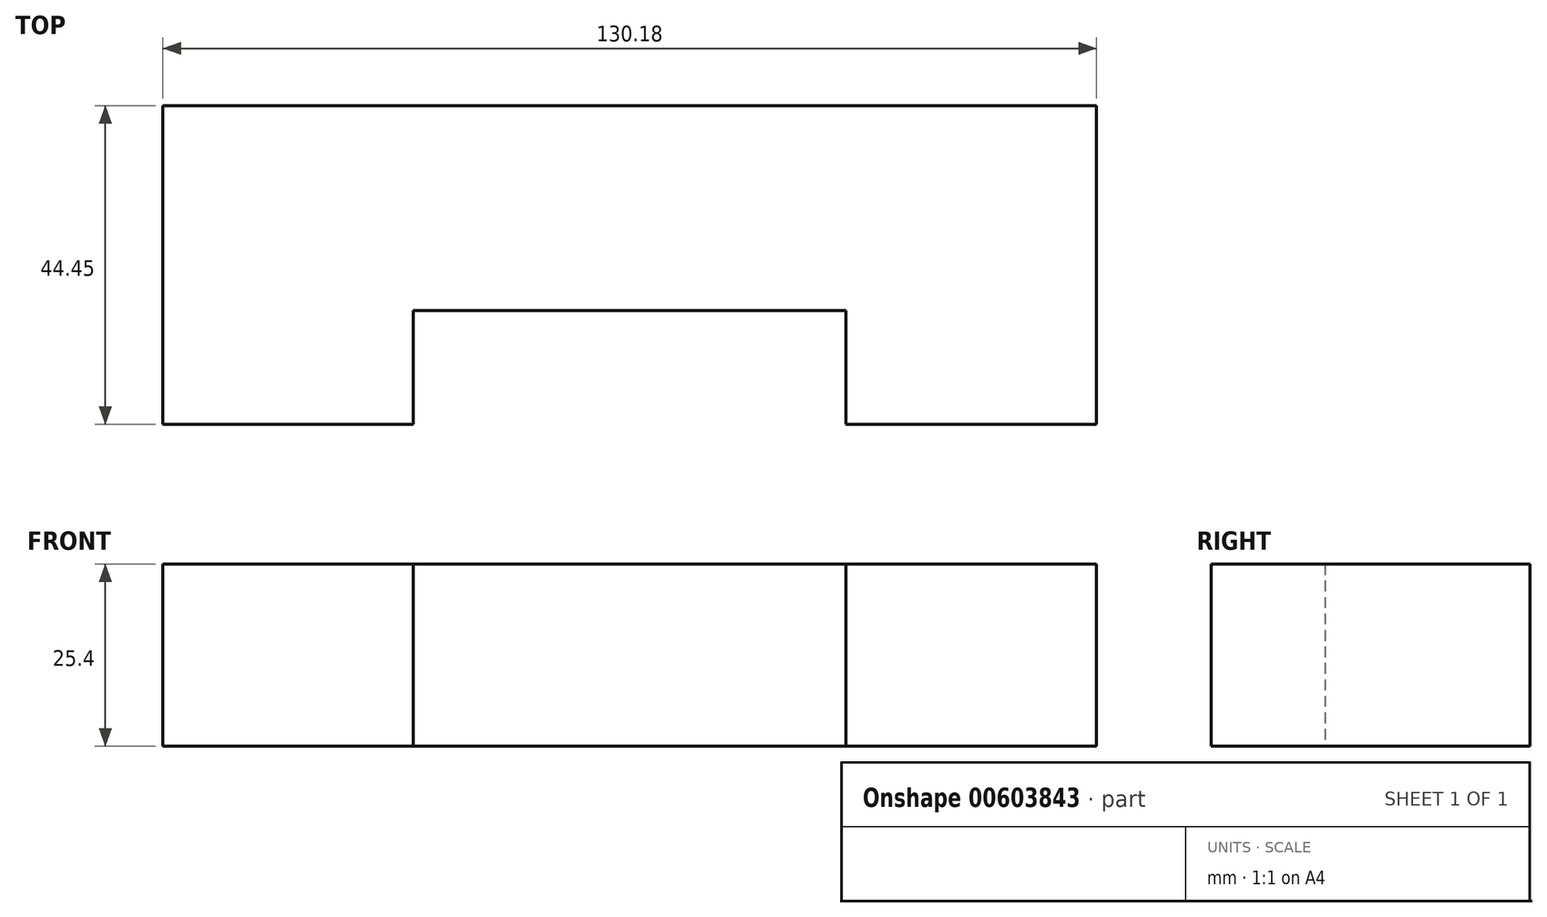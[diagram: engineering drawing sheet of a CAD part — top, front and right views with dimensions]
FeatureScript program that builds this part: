
annotation { "Feature Type Name" : "Feature", "Feature Type Description" : "" }
export const myFeature = defineFeature(function(context is Context, id is Id, definition is map)
    precondition{}
    {
        {
            var Q0;
            Q0=qCreatedBy(makeId("Top.planeOp"),FACE);
            var sketch = newSketch(context, id + "F0", { "sketchPlane" : qUnion([Q0])});
            skLineSegment(sketch, "E0", {"start": v(-58.79, 51.02) * mm, "end": v(71.39, 51.02) * mm});
            skLineSegment(sketch, "E1", {"start": v(-58.79, 51.02) * mm, "end": v(-58.79, 6.57) * mm});
            skLineSegment(sketch, "E2", {"start": v(71.39, 51.02) * mm, "end": v(71.39, 6.57) * mm});
            skLineSegment(sketch, "E3", {"start": v(71.39, 6.57) * mm, "end": v(-58.79, 6.57) * mm});
            skLineSegment(sketch, "E4", {"start": v(71.39, 6.57) * mm, "end": v(36.46, 6.57) * mm});
            skLineSegment(sketch, "E5", {"start": v(-58.79, 6.57) * mm, "end": v(-23.86, 6.57) * mm});
            skLineSegment(sketch, "E6", {"start": v(36.46, 6.57) * mm, "end": v(36.46, 22.44) * mm});
            skLineSegment(sketch, "E7", {"start": v(-23.86, 6.57) * mm, "end": v(-23.86, 22.44) * mm});
            skLineSegment(sketch, "E8", {"start": v(-23.86, 22.44) * mm, "end": v(36.46, 22.44) * mm});
            skSolve(sketch);
        }
        {
            var Q0;
            Q0=makeQuery(id+"F0.imprint","IMPRINT",FACE,{"disambiguationData":[TD([[makeQuery(id+"F0.imprint","IMPRINT",EDGE,{"derivedFrom":sQuery(id+"F0.wireOp",EDGE,"E3")}),-1.0]])]});
            var Q1;
            Q1=makeQuery(id+"F0.imprint","IMPRINT",FACE,{"disambiguationData":[TD([[makeQuery(id+"F0.imprint","IMPRINT",EDGE,{"derivedFrom":sQuery(id+"F0.wireOp",EDGE,"E0")}),-1.0]])]});
            extrude(context, id + "F1", {"entities" : qUnion([Q0, Q1]), "depth" : 25.4 * mm, "offsetDistance" : 25.4 * mm});
        }
    });
